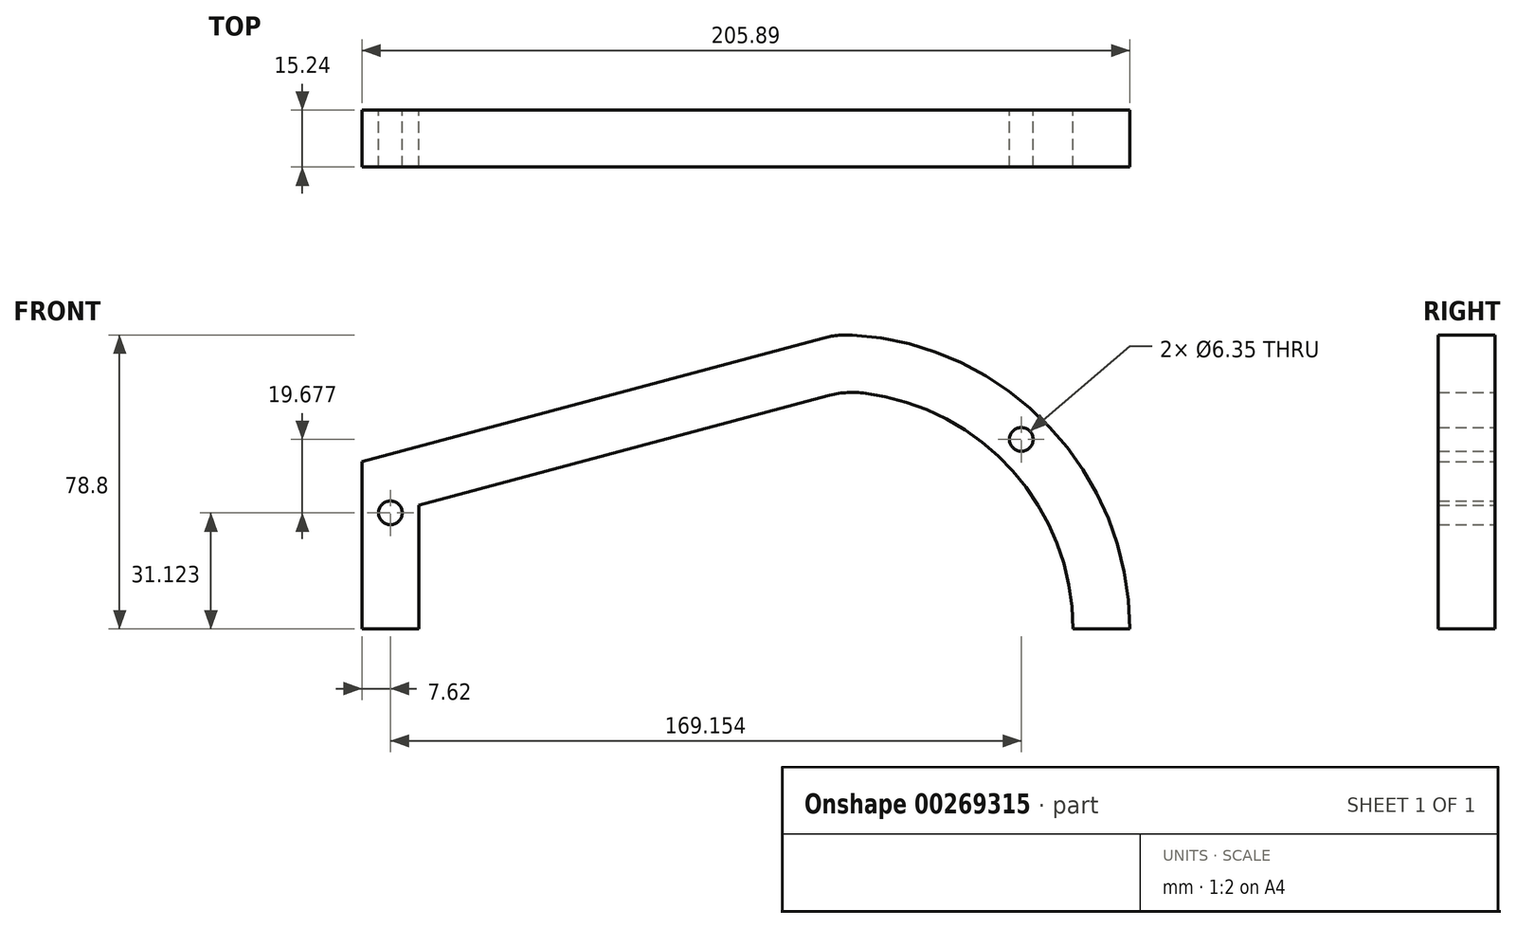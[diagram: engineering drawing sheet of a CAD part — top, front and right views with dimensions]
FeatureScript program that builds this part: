
annotation { "Feature Type Name" : "Feature", "Feature Type Description" : "" }
export const myFeature = defineFeature(function(context is Context, id is Id, definition is map)
    precondition{}
    {
        {
            var Q0;
            Q0=qCreatedBy(makeId("Front.planeOp"),FACE);
            var sketch = newSketch(context, id + "F0", { "sketchPlane" : qUnion([Q0])});
            skArc(sketch, "E0", {"start": v(78.89, 0) * mm, "mid": v(57.34, 54.18) * mm, "end": v(4.46, 78.76) * mm});
            skLineSegment(sketch, "E1", {"start": v(0, -78.89) * mm, "end": v(-588.83, -78.89) * mm, "construction": true});
            skLineSegment(sketch, "E2", {"start": v(-588.83, -78.89) * mm, "end": v(-3.55, 77.94) * mm, "construction": true});
            skArc(sketch, "E3.0", {"start": v(63.65, 0) * mm, "mid": v(47.53, 42.34) * mm, "end": v(7.33, 63.23) * mm});
            skLineSegment(sketch, "E4.bottom", {"start": v(78.89, 0) * mm, "end": v(-141.11, 0) * mm, "construction": true});
            skLineSegment(sketch, "E4.top", {"start": v(78.89, 140) * mm, "end": v(-141.11, 140) * mm, "construction": true});
            skLineSegment(sketch, "E4.left", {"start": v(78.89, 0) * mm, "end": v(78.89, 140) * mm, "construction": true});
            skLineSegment(sketch, "E4.right", {"start": v(-141.11, 0) * mm, "end": v(-141.11, 140) * mm, "construction": true});
            skLineSegment(sketch, "E5", {"start": v(78.89, 0) * mm, "end": v(63.65, 0) * mm});
            skLineSegment(sketch, "E6", {"start": v(-127, 0) * mm, "end": v(-127, 96.07) * mm, "construction": true});
            skLineSegment(sketch, "E7", {"start": v(-127, 0) * mm, "end": v(-127, 44.86) * mm});
            skLineSegment(sketch, "E8", {"start": v(-127, 44.86) * mm, "end": v(0, 78.89) * mm});
            skLineSegment(sketch, "E9", {"start": v(-111.76, 0) * mm, "end": v(-111.76, 33.16) * mm});
            skLineSegment(sketch, "E10", {"start": v(-111.76, 33.16) * mm, "end": v(-2.17, 62.53) * mm});
            skPoint(sketch, "E11.visualSharp", {"position": v(0, 78.89) * mm});
            skArc(sketch, "E11.filletArc", {"start": v(4.46, 78.76) * mm, "mid": v(0.42, 78.67) * mm, "end": v(-3.55, 77.94) * mm});
            skPoint(sketch, "E12.visualSharp", {"position": v(1.9, 63.62) * mm});
            skArc(sketch, "E12.filletArc", {"start": v(7.33, 63.23) * mm, "mid": v(2.54, 63.33) * mm, "end": v(-2.17, 62.53) * mm});
            skLineSegment(sketch, "E13", {"start": v(-127, 0) * mm, "end": v(-111.76, 0) * mm});
            skCircle(sketch, "E14", {"center": v(-119.38, 31.12) * mm, "radius": 3.18 * mm});
            skCircle(sketch, "E15", {"center": v(49.77, 50.8) * mm, "radius": 3.18 * mm});
            skSolve(sketch);
        }
        {
            var Q0;
            Q0 = qSketchRegion(id + "F0", true);
            extrude(context, id + "F1", {"entities" : qUnion([Q0]), "depth" : 15.24 * mm});
        }
    });
